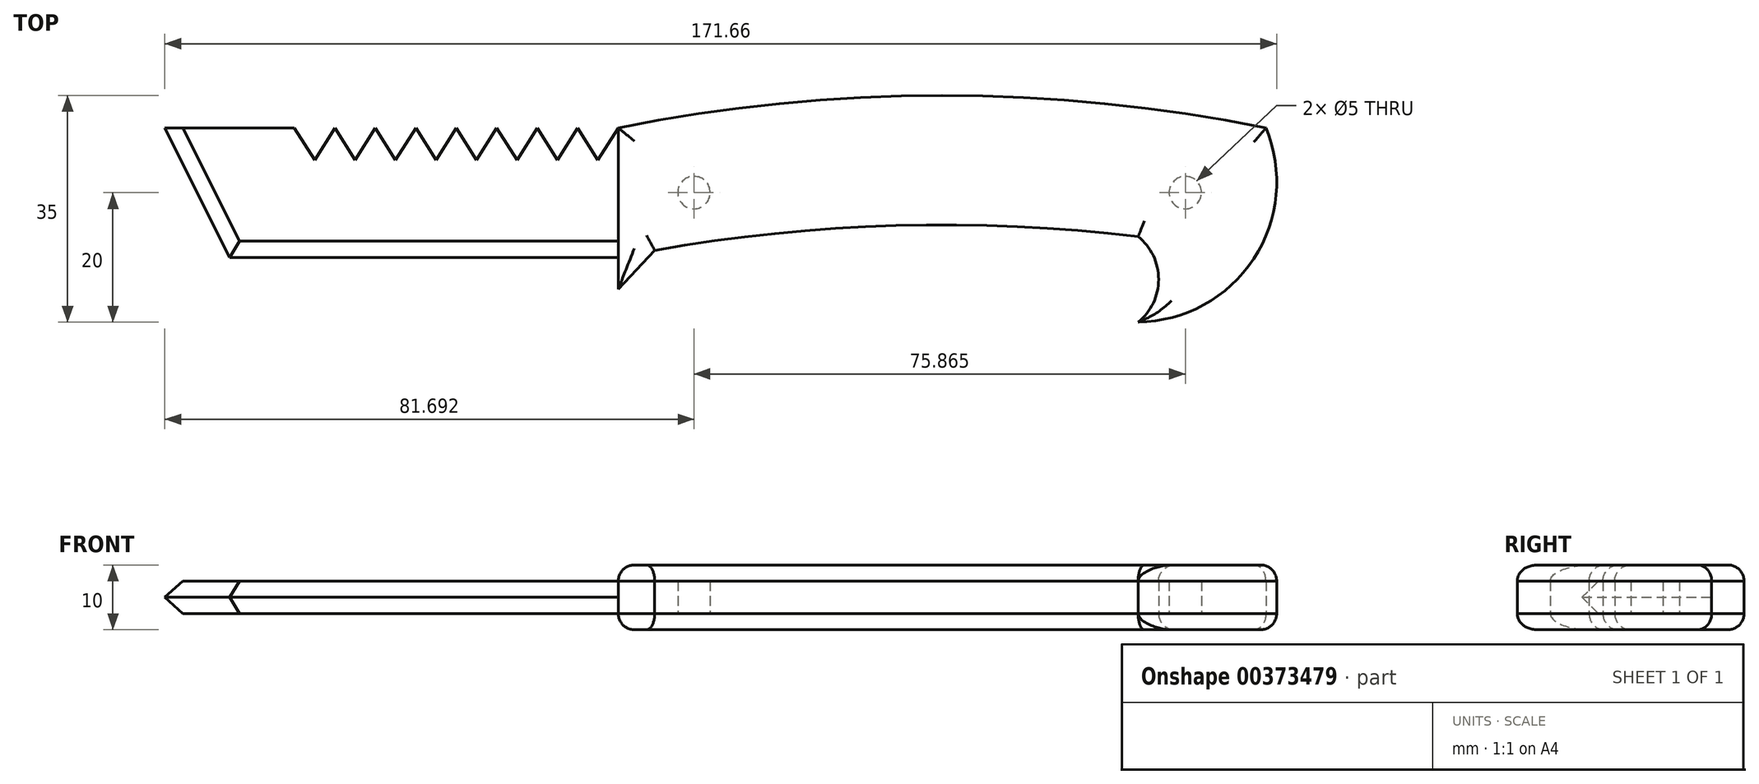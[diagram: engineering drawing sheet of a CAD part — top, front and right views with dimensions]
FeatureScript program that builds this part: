
annotation { "Feature Type Name" : "Feature", "Feature Type Description" : "" }
export const myFeature = defineFeature(function(context is Context, id is Id, definition is map)
    precondition{}
    {
        {
            var Q0;
            Q0=qCreatedBy(makeId("Top.planeOp"),FACE);
            var sketch = newSketch(context, id + "F0", { "sketchPlane" : qUnion([Q0])});
            skLineSegment(sketch, "E0.top", {"start": v(-25.3, 15.54) * mm, "end": v(34.7, 15.54) * mm});
            skLineSegment(sketch, "E0.right", {"start": v(34.7, 35.54) * mm, "end": v(34.7, 15.54) * mm});
            skLineSegment(sketch, "E1", {"start": v(-35.3, 35.54) * mm, "end": v(-25.3, 15.54) * mm});
            skArc(sketch, "E2", {"start": v(134.7, 35.54) * mm, "mid": v(84.7, 40.54) * mm, "end": v(34.7, 35.54) * mm});
            skPoint(sketch, "E3", {"position": v(114.96, 18.75) * mm});
            skArc(sketch, "E4", {"start": v(114.96, 18.75) * mm, "mid": v(74.7, 20.36) * mm, "end": v(34.7, 15.54) * mm});
            skArc(sketch, "E5", {"start": v(114.96, 5.54) * mm, "mid": v(118.13, 12.15) * mm, "end": v(114.96, 18.75) * mm});
            skArc(sketch, "E6", {"start": v(114.96, 5.54) * mm, "mid": v(132.8, 15.3) * mm, "end": v(134.7, 35.54) * mm});
            skLineSegment(sketch, "E7.right", {"start": v(34.7, 35.54) * mm, "end": v(34.7, 30.54) * mm});
            skPoint(sketch, "E8", {"position": v(9.7, 30.54) * mm});
            skPoint(sketch, "E9", {"position": v(-2.8, 30.54) * mm});
            skPoint(sketch, "E10", {"position": v(22.2, 30.54) * mm});
            skPoint(sketch, "E11", {"position": v(-9.05, 30.54) * mm});
            skPoint(sketch, "E12", {"position": v(3.45, 30.54) * mm});
            skPoint(sketch, "E13", {"position": v(15.95, 30.54) * mm});
            skPoint(sketch, "E14", {"position": v(28.45, 30.54) * mm});
            skPoint(sketch, "E15", {"position": v(-12.18, 30.54) * mm});
            skPoint(sketch, "E16", {"position": v(-5.93, 30.54) * mm});
            skPoint(sketch, "E17", {"position": v(0.32, 30.54) * mm});
            skPoint(sketch, "E18", {"position": v(6.57, 30.54) * mm});
            skPoint(sketch, "E19", {"position": v(12.82, 30.54) * mm});
            skPoint(sketch, "E20", {"position": v(19.07, 30.54) * mm});
            skPoint(sketch, "E21", {"position": v(25.32, 30.54) * mm});
            skPoint(sketch, "E22", {"position": v(31.57, 30.54) * mm});
            skLineSegment(sketch, "E23", {"start": v(-12.18, 30.54) * mm, "end": v(-15.3, 35.54) * mm});
            skLineSegment(sketch, "E24", {"start": v(-12.18, 30.54) * mm, "end": v(-9.05, 35.54) * mm});
            skLineSegment(sketch, "E25", {"start": v(-9.05, 35.54) * mm, "end": v(-5.93, 30.54) * mm});
            skLineSegment(sketch, "E26", {"start": v(-5.93, 30.54) * mm, "end": v(-2.8, 35.54) * mm});
            skLineSegment(sketch, "E27", {"start": v(-2.8, 35.54) * mm, "end": v(0.32, 30.54) * mm});
            skLineSegment(sketch, "E28", {"start": v(0.32, 30.54) * mm, "end": v(3.45, 35.54) * mm});
            skLineSegment(sketch, "E29", {"start": v(3.45, 35.54) * mm, "end": v(6.57, 30.54) * mm});
            skLineSegment(sketch, "E30", {"start": v(6.57, 30.54) * mm, "end": v(9.7, 35.54) * mm});
            skLineSegment(sketch, "E31", {"start": v(9.7, 35.54) * mm, "end": v(12.82, 30.54) * mm});
            skLineSegment(sketch, "E32", {"start": v(12.82, 30.54) * mm, "end": v(15.95, 35.54) * mm});
            skLineSegment(sketch, "E33", {"start": v(15.95, 35.54) * mm, "end": v(19.07, 30.54) * mm});
            skLineSegment(sketch, "E34", {"start": v(19.07, 30.54) * mm, "end": v(22.2, 35.54) * mm});
            skLineSegment(sketch, "E35", {"start": v(22.2, 35.54) * mm, "end": v(25.32, 30.54) * mm});
            skLineSegment(sketch, "E36", {"start": v(25.32, 30.54) * mm, "end": v(28.45, 35.54) * mm});
            skLineSegment(sketch, "E37", {"start": v(28.45, 35.54) * mm, "end": v(31.57, 30.54) * mm});
            skLineSegment(sketch, "E38", {"start": v(31.57, 30.54) * mm, "end": v(34.7, 35.54) * mm});
            skLineSegment(sketch, "E39", {"start": v(-35.3, 35.54) * mm, "end": v(-15.3, 35.54) * mm});
            skPoint(sketch, "E40", {"position": v(-30.3, 25.54) * mm});
            skPoint(sketch, "E41", {"position": v(46.4, 25.54) * mm});
            skCircle(sketch, "E42", {"center": v(46.4, 25.54) * mm, "radius": 2.5 * mm});
            skPoint(sketch, "E43", {"position": v(122.26, 25.54) * mm});
            skCircle(sketch, "E44", {"center": v(122.26, 25.54) * mm, "radius": 2.5 * mm});
            skLineSegment(sketch, "E45.left", {"start": v(34.7, 35.54) * mm, "end": v(34.7, 10.63) * mm});
            skPoint(sketch, "E46", {"position": v(40.33, 16.61) * mm});
            skLineSegment(sketch, "E47", {"start": v(34.7, 10.63) * mm, "end": v(40.33, 16.61) * mm});
            skSolve(sketch);
        }
        {
            var Q0;
            {var subQ6=sQuery(id+"F0.wireOp",EDGE,"E2");Q0=makeQuery(id+"F0.imprint","IMPRINT",FACE,{"disambiguationData":[TD([[makeQuery(id+"F0.imprint","IMPRINT",EDGE,{"derivedFrom":subQ6}),1.0]])]});}
            var Q1;
            {var subQ3=sQuery(id+"F0.wireOp",EDGE,"E47");Q1=makeQuery(id+"F0.imprint","IMPRINT",FACE,{"disambiguationData":[TD([[makeQuery(id+"F0.imprint","IMPRINT",EDGE,{"derivedFrom":subQ3}),1.0]])]});}
            var Q2;
            Q2=makeQuery(id+"F0.imprint","IMPRINT",FACE,{"disambiguationData":[TD([[makeQuery(id+"F0.imprint","IMPRINT",EDGE,{"derivedFrom":sQuery(id+"F0.wireOp",EDGE,"E42")}),1.0]])]});
            var Q3;
            Q3=makeQuery(id+"F0.imprint","IMPRINT",FACE,{"disambiguationData":[TD([[makeQuery(id+"F0.imprint","IMPRINT",EDGE,{"derivedFrom":sQuery(id+"F0.wireOp",EDGE,"E44")}),1.0]])]});
            extrude(context, id + "F1", {"entities" : qUnion([Q0, Q1, Q2, Q3]), "depth" : 5 * mm, "hasSecondDirection" : true, "secondDirectionOppositeDirection" : true, "secondDirectionDepth" : 5 * mm});
        }
        {
            var Q0;
            Q0=makeQuery(id+"F0.imprint","IMPRINT",FACE,{"disambiguationData":[TD([[makeQuery(id+"F0.imprint","IMPRINT",EDGE,{"derivedFrom":sQuery(id+"F0.wireOp",EDGE,"E0.top")}),1.0]])]});
            var Q1;
            {var subQ2=sQuery(id+"F0.wireOp",EDGE,"E2");Q1=makeQuery(id+"F0.imprint","IMPRINT",FACE,{"disambiguationData":[TD([[makeQuery(id+"F0.imprint","IMPRINT",EDGE,{"derivedFrom":subQ2}),1.0]])]});}
            var Q2;
            {var subQ4=sQuery(id+"F0.wireOp",EDGE,"E45.top");Q2=makeQuery(id+"F0.imprint","IMPRINT",FACE,{"disambiguationData":[TD([[makeQuery(id+"F0.imprint","IMPRINT",EDGE,{"derivedFrom":subQ4}),1.0]])]});}
            var Q3;
            {var subQ3=sQuery(id+"F0.wireOp",EDGE,"E47");Q3=makeQuery(id+"F0.imprint","IMPRINT",FACE,{"disambiguationData":[TD([[makeQuery(id+"F0.imprint","IMPRINT",EDGE,{"derivedFrom":subQ3}),1.0]])]});}
            extrude(context, id + "F2", {"entities" : qUnion([Q0, Q1, Q2, Q3]), "depth" : 2.5 * mm, "hasSecondDirection" : true, "secondDirectionOppositeDirection" : true, "secondDirectionDepth" : 2.5 * mm});
        }
        {
            var Q0;
            Q0=makeQuery(id+"F2.opExtrude","CAP_EDGE",EDGE,{"disambiguationData":[OSD([sQuery(id+"F0.wireOp",EDGE,"E1")])],"isStart":false});
            var Q1;
            Q1=makeQuery(id+"F2.opExtrude","CAP_EDGE",EDGE,{"disambiguationData":[OSD([sQuery(id+"F0.wireOp",EDGE,"E0.top")])],"isStart":false});
            var Q2;
            Q2=makeQuery(id+"F2.opExtrude","CAP_EDGE",EDGE,{"disambiguationData":[OSD([sQuery(id+"F0.wireOp",EDGE,"E1")])],"isStart":true});
            var Q3;
            Q3=makeQuery(id+"F2.opExtrude","CAP_EDGE",EDGE,{"disambiguationData":[OSD([sQuery(id+"F0.wireOp",EDGE,"E0.top")])],"isStart":true});
            chamfer(context, id + "F3", {"entities" : qUnion([Q0, Q1, Q2, Q3]), "width" : 2.5 * mm, "tangentPropagation" : true});
        }
        {
            var Q0;
            Q0=makeQuery(id+"F1.opExtrude","CAP_EDGE",EDGE,{"disambiguationData":[OSD([sQuery(id+"F0.wireOp",EDGE,"E4")])],"isStart":false});
            var Q1;
            Q1=makeQuery(id+"F1.opExtrude","CAP_EDGE",EDGE,{"disambiguationData":[OSD([sQuery(id+"F0.wireOp",EDGE,"E47")])],"isStart":false});
            var Q2;
            Q2=makeQuery(id+"F1.opExtrude","CAP_EDGE",EDGE,{"disambiguationData":[OSD([sQuery(id+"F0.wireOp",EDGE,"E45.left")])],"isStart":false});
            var Q3;
            Q3=makeQuery(id+"F1.opExtrude","CAP_EDGE",EDGE,{"disambiguationData":[OSD([sQuery(id+"F0.wireOp",EDGE,"E2")])],"isStart":false});
            var Q4;
            Q4=makeQuery(id+"F1.opExtrude","CAP_EDGE",EDGE,{"disambiguationData":[OSD([sQuery(id+"F0.wireOp",EDGE,"E6")])],"isStart":false});
            var Q5;
            Q5=makeQuery(id+"F1.opExtrude","CAP_EDGE",EDGE,{"disambiguationData":[OSD([sQuery(id+"F0.wireOp",EDGE,"E5")])],"isStart":false});
            var Q6;
            Q6=makeQuery(id+"F1.opExtrude","CAP_EDGE",EDGE,{"disambiguationData":[OSD([sQuery(id+"F0.wireOp",EDGE,"E5")])],"isStart":true});
            var Q7;
            Q7=makeQuery(id+"F1.opExtrude","CAP_EDGE",EDGE,{"disambiguationData":[OSD([sQuery(id+"F0.wireOp",EDGE,"E4")])],"isStart":true});
            var Q8;
            Q8=makeQuery(id+"F1.opExtrude","CAP_EDGE",EDGE,{"disambiguationData":[OSD([sQuery(id+"F0.wireOp",EDGE,"E45.left")])],"isStart":true});
            var Q9;
            Q9=makeQuery(id+"F1.opExtrude","CAP_EDGE",EDGE,{"disambiguationData":[OSD([sQuery(id+"F0.wireOp",EDGE,"E47")])],"isStart":true});
            var Q10;
            Q10=makeQuery(id+"F1.opExtrude","CAP_EDGE",EDGE,{"disambiguationData":[OSD([sQuery(id+"F0.wireOp",EDGE,"E2")])],"isStart":true});
            var Q11;
            Q11=makeQuery(id+"F1.opExtrude","CAP_EDGE",EDGE,{"disambiguationData":[OSD([sQuery(id+"F0.wireOp",EDGE,"E6")])],"isStart":true});
            fillet(context, id + "F4", {"entities" : qUnion([Q0, Q1, Q2, Q3, Q4, Q5, Q6, Q7, Q8, Q9, Q10, Q11]), "radius" : 2.5 * mm, "tangentPropagation" : true, "allowEdgeOverflow" : false});
        }
    });
